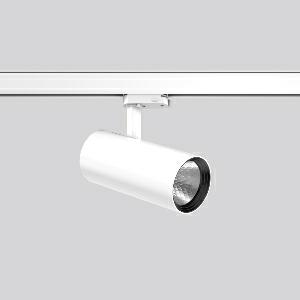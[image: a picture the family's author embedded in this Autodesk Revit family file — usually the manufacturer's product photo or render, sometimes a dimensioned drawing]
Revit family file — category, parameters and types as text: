
# Revit family: deecos_s_mini_742195_002_1_76_ae09
name_source: partatom
category: Lighting Fixtures
units: mm (PartAtom-declared; Revit-internal decimal feet)

## family parameters
Cut with Voids When Loaded = No
Host = Face
Light Source = No
Part Type = Normal
Room Calculation Point = No
Round Connector Dimension = Use Diameter
Shared = No

## types (1)
- DEECOS S mini (1 x LED Modul 940, 2700 lm, 4000)
    Apparent Load = 20 VA
    Approval mark = CE
    CIE Flux Codes = 100 100 100 100 100
    Color Rendering = 92
    Color Temperature = 4000
    Default Elevation = 1800 mm
    Description = Series: DEECOS S mini
LED surface-mounted projector in modern design with no visible cooling ribs. Housing: die-cast aluminium, powder-coated. Rotation range: 356°. Swivel range: 90°. Black plastic ring and recessed LED to prevent glare from the side. Optical assembly with reflector made of MIRO-Silver with 98% total light reflection for outstanding efficiency - can be changed without tools. Best colour rendering index Ra>90. With adapter for RZB 3-circuit DALI tracks. Suitable for Track on ceiling, Wall track. High quality converter without flickering and stroboscopic effect. The following accessories can be mounted without use of tools: interchangeable lenses, decorative glasses, honeycomb louvre, clear and frosted diffusers, white interchangeable plastic ring. 
Colour: traffic white, matt (RAL 9016)
Diameter: 87 mm
Height: 214 mm
Lamp: LED
Socket: without socket
Colour temperature: 4000K
Colour rendering index (CRI): 92
System power: 20 W
Rated luminous flux: 2700 lm
Luminous efficiency: 135 lm/W
Control gear: Converter, dimmable, DALI
Protection class: I
Type of protection: IP 20
    Height = 214 mm
    Lamp = 1 x LED Modul 940
    Lamp Light Flux = 2700 lm
    Lamp count = 1
    Length = 87 mm
    Lifetime = 50000 h
    Luminous efficacy = 135 lm/W
    Manufacturer = RZB
    ModVariant = No
    Model = 742195.002.1.76
    Mounting Place = Ceiling
    Mounting Type = Rail mounted
    Number of Poles = 1
    OnlyDefault = Yes
    Power Factor = 1
    Product Name = DEECOS S mini
    Product group = Track mounted projectors
    ProductGroupID = 301
    Protection Class = Protection class I
    Protection Degree = IP 20
    RLX_Detail_Level = 1
    RLX_Emergency_Light_Flux = 0 lm
    RLX_Emergency_Type = 0
    RLX_Emergency_Type_DB = No
    RlxData = <blob elided: 35065 chars, md5=6da91c0f>
    Socket = socket
    Standby Power = 0 W
    System Light Flux = 2700 lm
    System Power = 20 W
    Type Comments = Product without accessories
    Type Image = 741926.002.jpg
    URL = http://relux.com
    VarID = ---
    Voltage = 230 V
    Voltage Range = 220-240 V
    Weight = 0.00 kg
    Width = 0 mm  [stored 0 ft]

note: [stored X ft] marks values corroborated as IEEE doubles in the binary element streams (Revit-internal decimal feet)

## geometry (parser evidence)
native form markers: Blend x4, Sweep x11
no freeform markers — native parametric forms only
